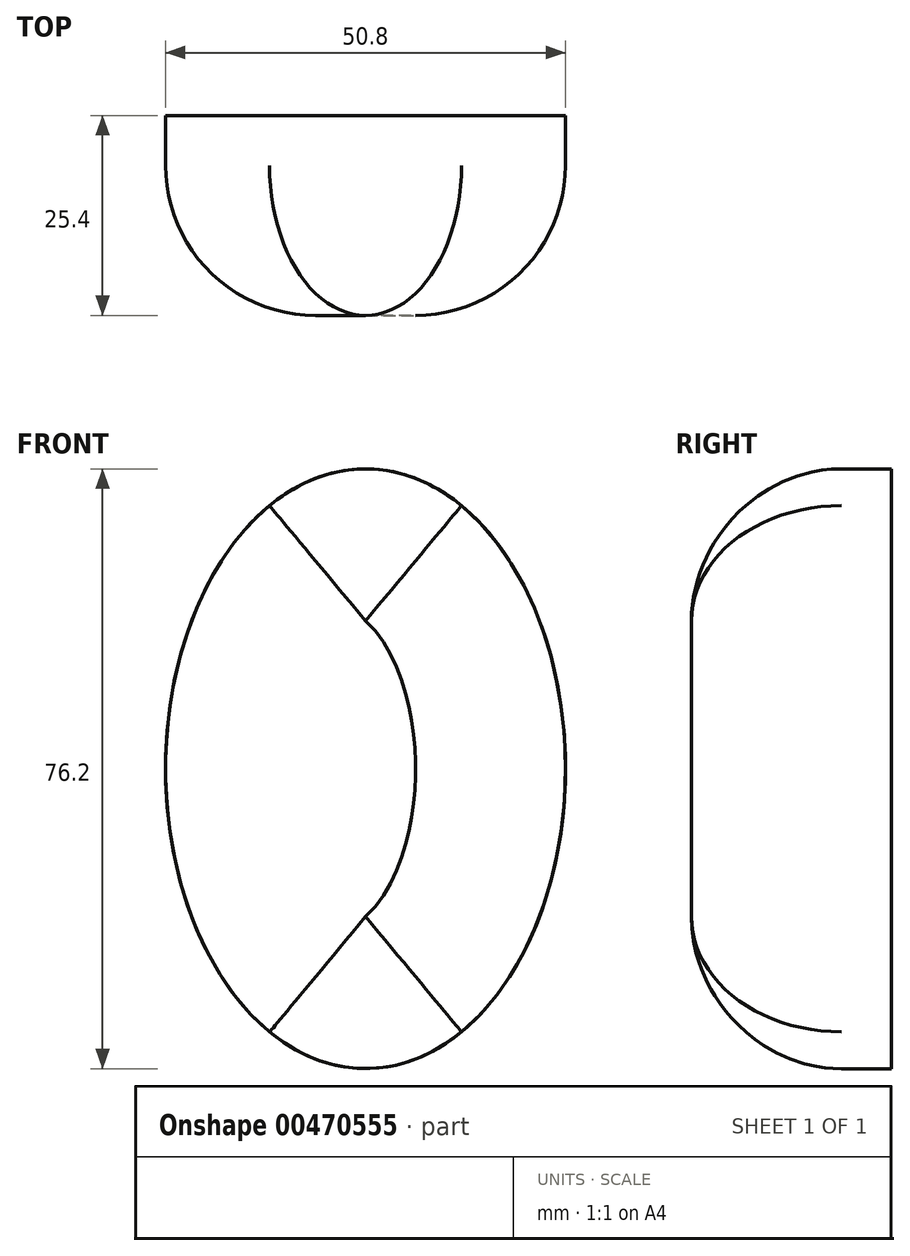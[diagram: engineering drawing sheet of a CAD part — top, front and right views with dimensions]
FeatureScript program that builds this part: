
annotation { "Feature Type Name" : "Feature", "Feature Type Description" : "" }
export const myFeature = defineFeature(function(context is Context, id is Id, definition is map)
    precondition{}
    {
        {
            var Q0;
            Q0=qCreatedBy(makeId("Front.planeOp"),FACE);
            var sketch = newSketch(context, id + "F0", { "sketchPlane" : qUnion([Q0])});
            skEllipse(sketch, "E0", {"center": v(0, 0) * mm, "majorRadius": 38.1 * mm, "minorRadius": 25.4 * mm, "majorAxis": v(0, 1)});
            skSolve(sketch);
        }
        {
            var Q0;
            Q0 = qSketchRegion(id + "F0", true);
            extrude(context, id + "F1", {"entities" : qUnion([Q0]), "depth" : 25.4 * mm});
        }
        {
            var Q0;
            Q0=makeQuery(id+"F1.opExtrude","CAP_EDGE",EDGE,{"disambiguationData":[OSD([sQuery(id+"F0.wireOp",EDGE,"E0")])],"isStart":false});
            fillet(context, id + "F2", {"entities" : qUnion([Q0]), "radius" : 19.05 * mm, "tangentPropagation" : true, "allowEdgeOverflow" : false});
        }
    });
